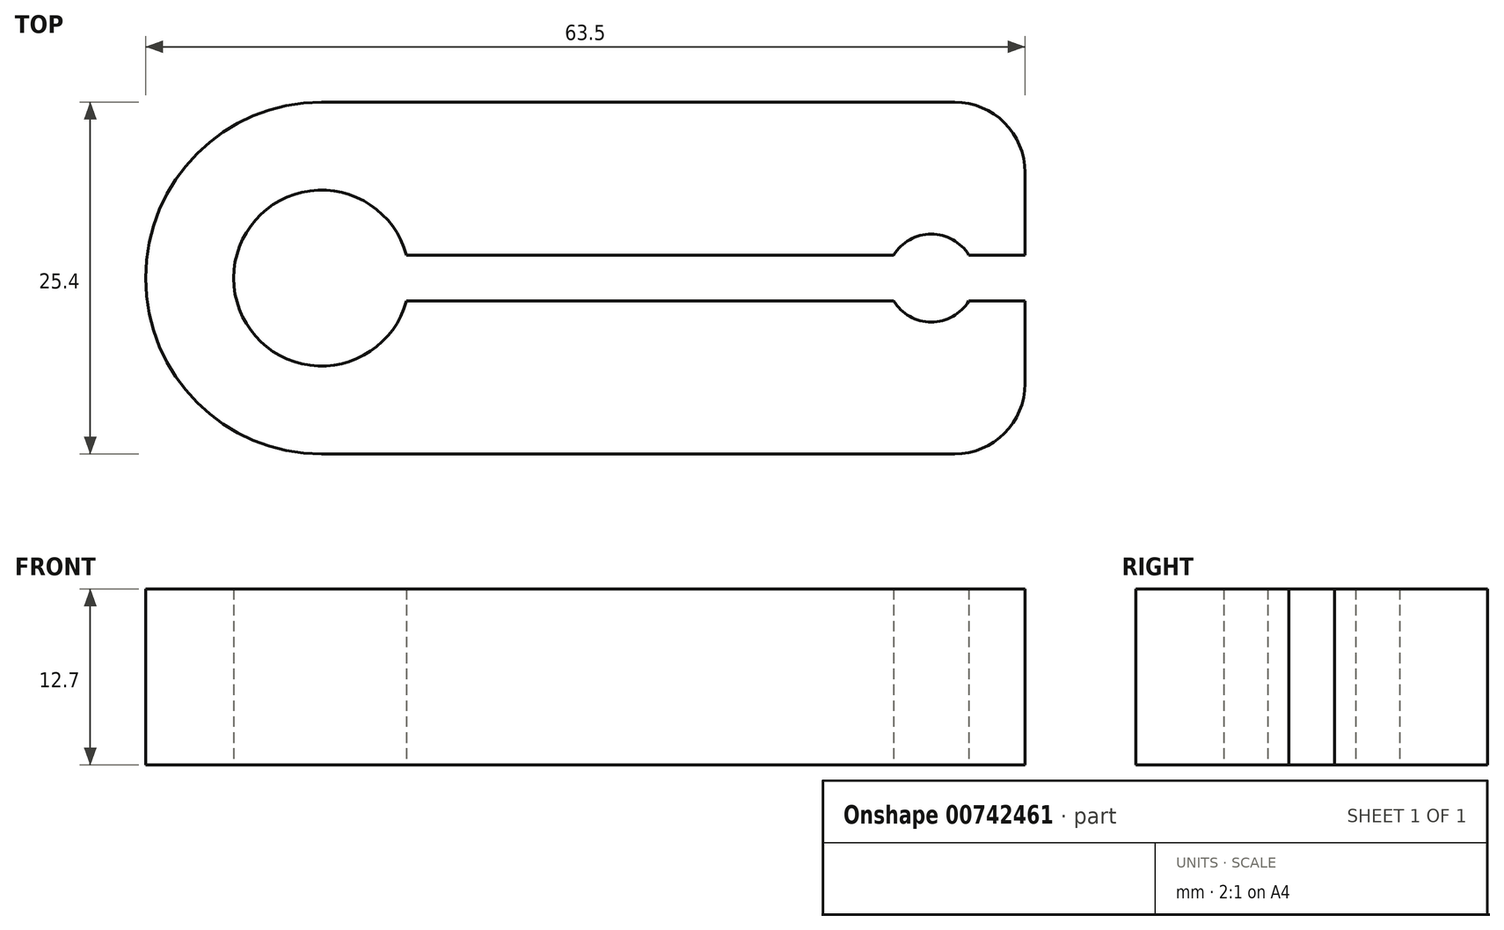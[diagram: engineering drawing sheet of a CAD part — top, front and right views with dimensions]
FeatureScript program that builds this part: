
annotation { "Feature Type Name" : "Feature", "Feature Type Description" : "" }
export const myFeature = defineFeature(function(context is Context, id is Id, definition is map)
    precondition{}
    {
        {
            var Q0;
            Q0=qCreatedBy(makeId("Top.planeOp"),FACE);
            var sketch = newSketch(context, id + "F0", { "sketchPlane" : qUnion([Q0])});
            skLineSegment(sketch, "E0.bottom", {"start": v(26.67, -12.7) * mm, "end": v(-19.05, -12.7) * mm});
            skLineSegment(sketch, "E0.top", {"start": v(26.67, 12.7) * mm, "end": v(-19.05, 12.7) * mm});
            skLineSegment(sketch, "E0.left", {"start": v(31.75, -7.62) * mm, "end": v(31.75, 7.62) * mm});
            skLineSegment(sketch, "E0.right", {"start": v(-31.75, 0) * mm, "end": v(-31.75, 0) * mm});
            skPoint(sketch, "E0.middle", {"position": v(0, 0) * mm});
            skPoint(sketch, "E1.visualSharp", {"position": v(-31.75, 12.7) * mm});
            skArc(sketch, "E1.filletArc", {"start": v(-19.05, 12.7) * mm, "mid": v(-28.03, 8.98) * mm, "end": v(-31.75, 0) * mm});
            skPoint(sketch, "E2.visualSharp", {"position": v(-31.75, -12.7) * mm});
            skArc(sketch, "E2.filletArc", {"start": v(-31.75, 0) * mm, "mid": v(-28.03, -8.98) * mm, "end": v(-19.05, -12.7) * mm});
            skPoint(sketch, "E3.visualSharp", {"position": v(31.75, 12.7) * mm});
            skArc(sketch, "E3.filletArc", {"start": v(31.75, 7.62) * mm, "mid": v(30.26, 11.21) * mm, "end": v(26.67, 12.7) * mm});
            skPoint(sketch, "E4.visualSharp", {"position": v(31.75, -12.7) * mm});
            skArc(sketch, "E4.filletArc", {"start": v(26.67, -12.7) * mm, "mid": v(30.26, -11.21) * mm, "end": v(31.75, -7.62) * mm});
            skCircle(sketch, "E5", {"center": v(24.98, 0) * mm, "radius": 3.18 * mm});
            skPoint(sketch, "E5.centerSnap0", {"position": v(31.75, 0) * mm});
            skCircle(sketch, "E6", {"center": v(-19.05, 0) * mm, "radius": 6.35 * mm});
            skLineSegment(sketch, "E7.bottom", {"start": v(31.75, 1.65) * mm, "end": v(-19.05, 1.65) * mm});
            skLineSegment(sketch, "E7.top", {"start": v(31.75, -1.65) * mm, "end": v(-19.05, -1.65) * mm});
            skLineSegment(sketch, "E7.left", {"start": v(31.75, 1.65) * mm, "end": v(31.75, -1.65) * mm});
            skLineSegment(sketch, "E7.right", {"start": v(-19.05, 1.65) * mm, "end": v(-19.05, -1.65) * mm});
            skSolve(sketch);
        }
        {
            var Q0;
            Q0=makeQuery(id+"F0.imprint","IMPRINT",FACE,{"disambiguationData":[TD([[makeQuery(id+"F0.imprint","IMPRINT",EDGE,{"derivedFrom":sQuery(id+"F0.wireOp",EDGE,"E0.bottom")}),-1.0]])]});
            extrude(context, id + "F1", {"entities" : qUnion([Q0]), "depth" : 12.7 * mm, "offsetDistance" : 25.4 * mm});
        }
    });
